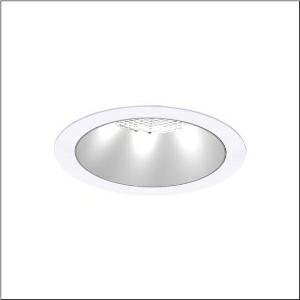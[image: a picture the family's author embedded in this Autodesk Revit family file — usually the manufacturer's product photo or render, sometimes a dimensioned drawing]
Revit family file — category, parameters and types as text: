
# Revit family: lunis_21_xl_51db19ef91c
name_source: partatom
category: Lighting Fixtures
units: mm (PartAtom-declared; Revit-internal decimal feet)

## family parameters
Cut with Voids When Loaded = No
Host = Face
Light Source = No
Part Type = Normal
Room Calculation Point = No
Round Connector Dimension = Use Diameter
Shared = No

## types (1)
- --- (1 x LED, 3900 lm, 25.4 W, 6500K)
    Apparent Load = 25 VA
    CIE Flux Codes = 91 99 100 100 100
    Color Rendering = 80
    Color Temperature = 6500K
    Default Elevation = 1800 mm
    Description = Lunis 21,  XL, downlight, light control with lens, of PMMA, anti glare with reflector, of PC, matt, light emission: direct distribution, LED rated luminous flux: 2.310lm, light colour: 830/840/865, with terminal, 5-pole, mains connection: 220..240V, AC/DC, 0/50..60Hz, housing, round, of diecast aluminium, traffic white (RAL 9016), diameter: 230mm, clamping range: 1..40mm, protection rating (complete): IP20, protection rating (on room side): IP54, insulation class (complete): insulation class II (safety insulation), certification: CE, impact resistance: IK03, packaging unit: 1 piece
    Height = 0 mm  [stored 0 ft]
    Lamp = 1 x LED
    Lamp Light Flux = 3900 lm
    Lamp Power = 25.4 W
    Lamp count = 1
    Length = 230 mm
    Luminous efficacy = 154 lm/W
    Manufacturer = Siteco
    ModVariant = No
    Model = 51DB19EF91C
    Mounting Place = Ceiling
    Mounting Type = Recessed
    Number of Poles = 1
    OnlyDefault = Yes
    Power Factor = 1
    Product Name = Lunis 21 XL
    Product group = downlight
    ProductGroupID = 401
    Protection Class = Protection class II
    Protection Degree = IP 20
    RLX_Detail_Level = 1
    RLX_Emergency_Light_Flux = 0 lm
    RLX_Emergency_Type = 0
    RLX_Emergency_Type_DB = No
    RlxData = <blob elided: 23017 chars, md5=00cdf85c>
    Socket = socket
    Standby Power = 0 W
    System Light Flux = 3900 lm
    System Power = 25 W
    Type Comments = individual setting: colour temperature 6500K, luminous flux: 100 % | (ON | ON | OFF | OFF) | 700 mA
    Type Image = l_1291163.jpg
    URL = http://relux.com
    VarID = @adj_038717
    Voltage = 0 V
    Weight = 0.00 kg
    Width = 0 mm  [stored 0 ft]

note: [stored X ft] marks values corroborated as IEEE doubles in the binary element streams (Revit-internal decimal feet)

## geometry (parser evidence)
native form markers: Blend x4, Sweep x9
no freeform markers — native parametric forms only
